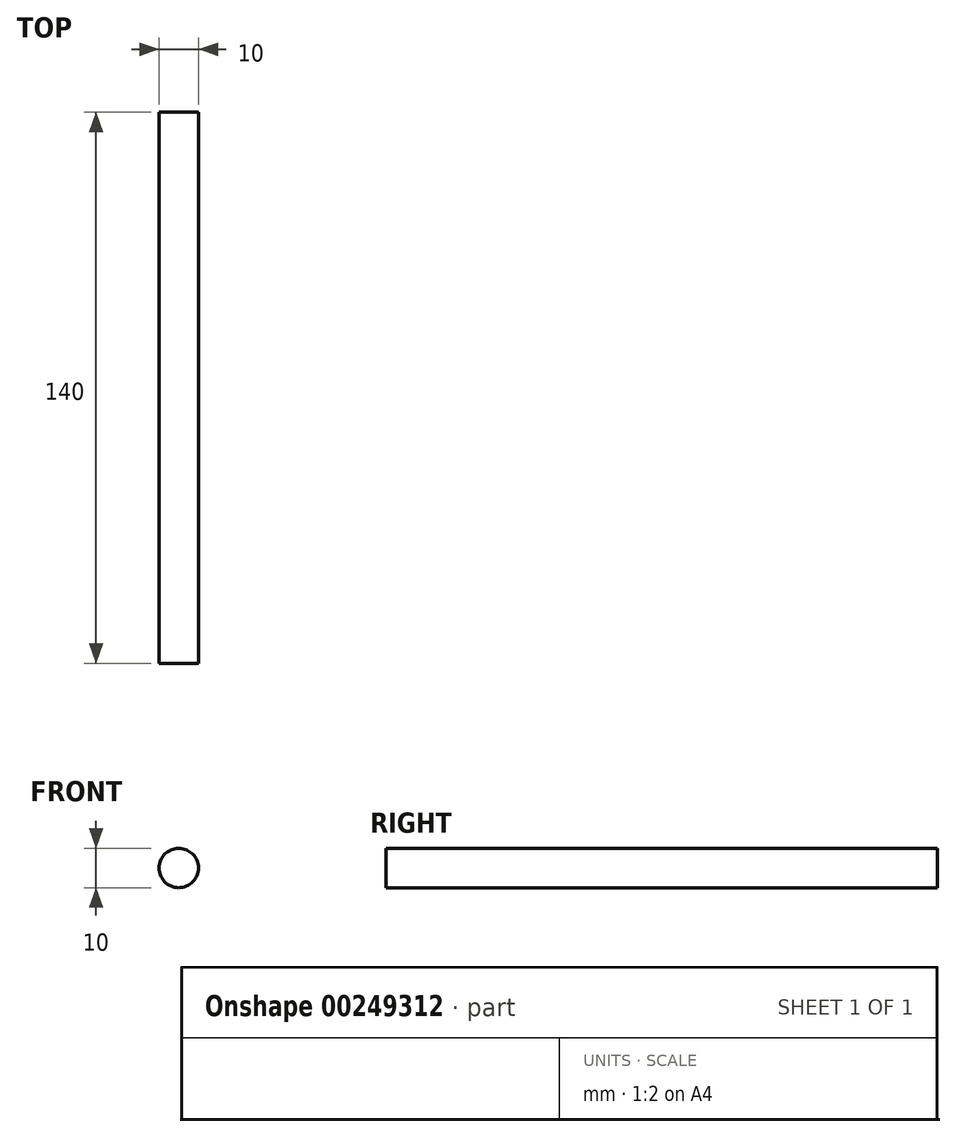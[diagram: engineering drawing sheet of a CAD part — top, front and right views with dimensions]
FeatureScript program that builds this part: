
annotation { "Feature Type Name" : "Feature", "Feature Type Description" : "" }
export const myFeature = defineFeature(function(context is Context, id is Id, definition is map)
    precondition{}
    {
        {
            var Q0;
            Q0=qCreatedBy(makeId("Front.planeOp"),FACE);
            var sketch = newSketch(context, id + "F0", { "sketchPlane" : qUnion([Q0])});
            skCircle(sketch, "E0", {"center": v(0, 0) * mm, "radius": 5 * mm});
            skSolve(sketch);
        }
        {
            var Q0;
            Q0=makeQuery(id+"F0.imprint","IMPRINT",FACE,{"disambiguationData":[TD([[makeQuery(id+"F0.imprint","IMPRINT",EDGE,{"derivedFrom":sQuery(id+"F0.wireOp",EDGE,"E0")}),1.0]])]});
            extrude(context, id + "F1", {"entities" : qUnion([Q0]), "depth" : 140 * mm, "offsetDistance" : 25 * mm});
        }
    });
